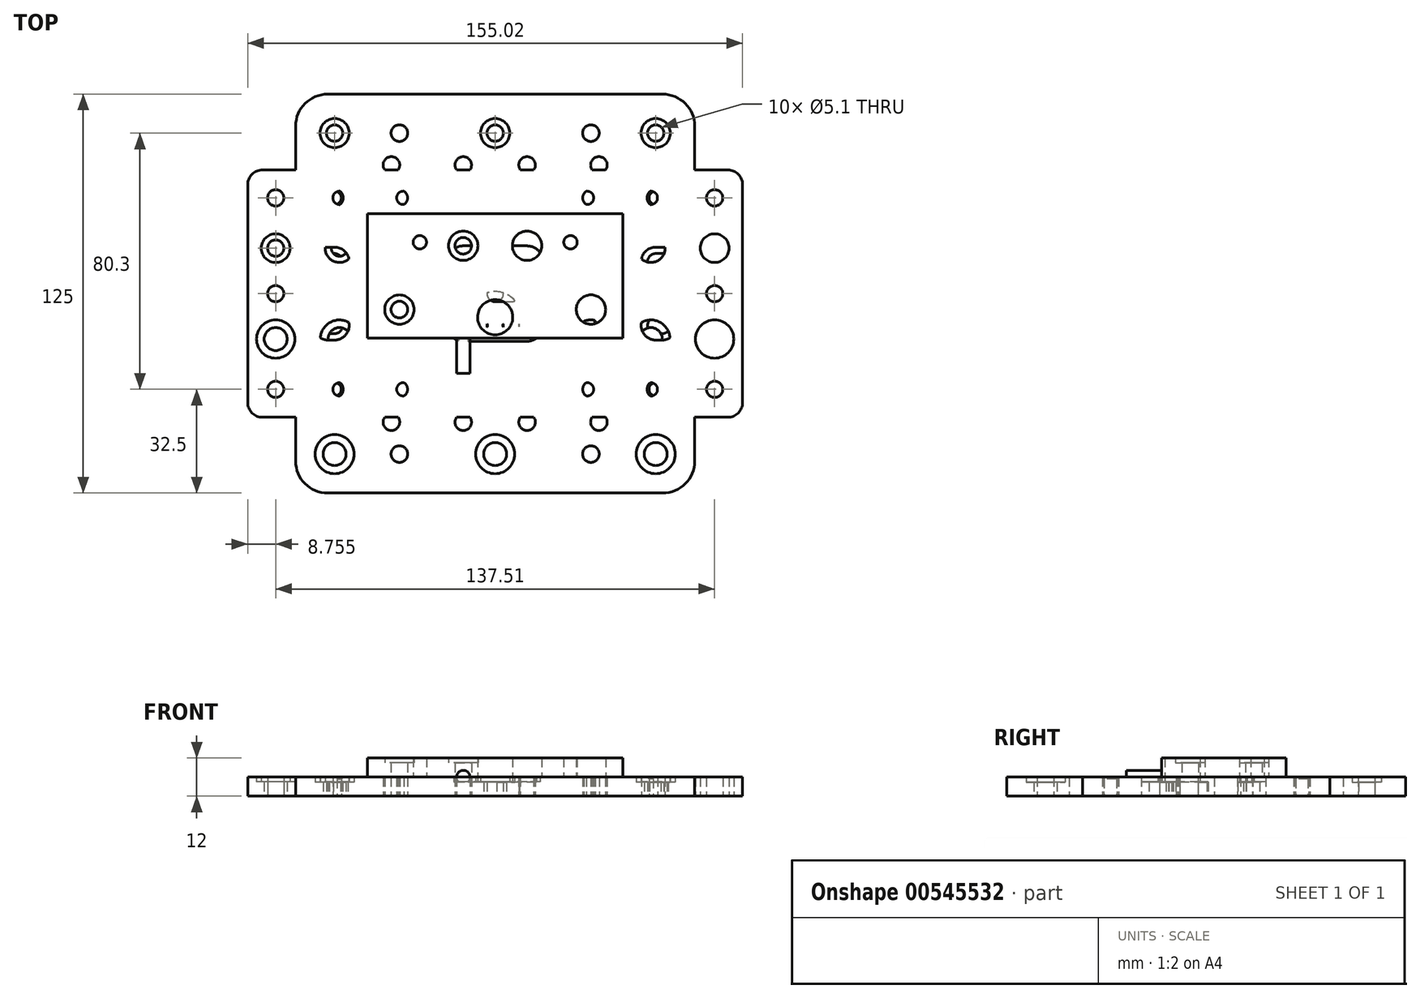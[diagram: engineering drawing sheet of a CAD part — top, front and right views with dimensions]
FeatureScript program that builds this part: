
annotation { "Feature Type Name" : "Feature", "Feature Type Description" : "" }
export const myFeature = defineFeature(function(context is Context, id is Id, definition is map)
    precondition{}
    {
        {
            assignVariable(context, id + "F0", {"name" : "CBeamEndPlateThickness", "anyValue" : 12});
        }
        {
            assignVariable(context, id + "F1", {"name" : "gantryPlateThickness", "anyValue" : 6});
        }
        {
            var Q0;
            Q0=qCreatedBy(makeId("Top.planeOp"),FACE);
            var sketch = newSketch(context, id + "F2", { "sketchPlane" : qUnion([Q0])});
            skLineSegment(sketch, "E0.bottom", {"start": v(-40, 25) * mm, "end": v(40, 25) * mm});
            skLineSegment(sketch, "E0.top", {"start": v(-40, -25) * mm, "end": v(40, -25) * mm});
            skLineSegment(sketch, "E0.left", {"start": v(-40, 25) * mm, "end": v(-40, -25) * mm});
            skLineSegment(sketch, "E0.right", {"start": v(40, 25) * mm, "end": v(40, -25) * mm});
            skPoint(sketch, "E0.middle", {"position": v(0, 0) * mm});
            skCircle(sketch, "E1", {"center": v(0, -7.4) * mm, "radius": 5.5 * mm});
            skCircle(sketch, "E2", {"center": v(0, -7.4) * mm, "radius": 8.05 * mm});
            skCircle(sketch, "E3", {"center": v(-30, -5) * mm, "radius": 2.6 * mm});
            skCircle(sketch, "E4", {"center": v(-30, -5) * mm, "radius": 4.6 * mm});
            skCircle(sketch, "E5", {"center": v(-23.6, 16.1) * mm, "radius": 2.1 * mm});
            skCircle(sketch, "E6", {"center": v(-10, 15) * mm, "radius": 2.6 * mm});
            skCircle(sketch, "E7", {"center": v(-10, 15) * mm, "radius": 4.6 * mm});
            skLineSegment(sketch, "E8", {"start": v(0, 0) * mm, "end": v(0, 25) * mm, "construction": true});
            skCircle(sketch, "E9.MirrorC", {"center": v(10, 15) * mm, "radius": 4.6 * mm});
            skCircle(sketch, "E10.MirrorC", {"center": v(10, 15) * mm, "radius": 2.6 * mm});
            skCircle(sketch, "E11.MirrorC", {"center": v(23.6, 16.1) * mm, "radius": 2.1 * mm});
            skCircle(sketch, "E12.MirrorC", {"center": v(30, -5) * mm, "radius": 4.6 * mm});
            skCircle(sketch, "E13.MirrorC", {"center": v(30, -5) * mm, "radius": 2.6 * mm});
            skSolve(sketch);
        }
        {
            var Q0;
            Q0=makeQuery(id+"F2.imprint","IMPRINT",FACE,{"disambiguationData":[TD([[makeQuery(id+"F2.imprint","IMPRINT",EDGE,{"derivedFrom":sQuery(id+"F2.wireOp",EDGE,"E0.bottom")}),-1.0]])]});
            extrude(context, id + "F3", {"entities" : qUnion([Q0]), "depth" : (getVariable(context, 'CBeamEndPlateThickness')) * mm, "offsetDistance" : 25 * mm});
        }
        {
            var Q0;
            Q0=makeQuery(id+"F2.imprint","IMPRINT",FACE,{"disambiguationData":[TD([[makeQuery(id+"F2.imprint","IMPRINT",EDGE,{"derivedFrom":sQuery(id+"F2.wireOp",EDGE,"E3")}),-1.0]])]});
            var Q1;
            Q1=makeQuery(id+"F2.imprint","IMPRINT",FACE,{"disambiguationData":[TD([[makeQuery(id+"F2.imprint","IMPRINT",EDGE,{"derivedFrom":sQuery(id+"F2.wireOp",EDGE,"E6")}),-1.0]])]});
            var Q2;
            Q2=makeQuery(id+"F2.imprint","IMPRINT",FACE,{"disambiguationData":[TD([[makeQuery(id+"F2.imprint","IMPRINT",EDGE,{"derivedFrom":sQuery(id+"F2.wireOp",EDGE,"E9.MirrorC")}),-1.0]])]});
            var Q3;
            Q3=makeQuery(id+"F2.imprint","IMPRINT",FACE,{"disambiguationData":[TD([[makeQuery(id+"F2.imprint","IMPRINT",EDGE,{"derivedFrom":sQuery(id+"F2.wireOp",EDGE,"E12.MirrorC")}),-1.0]])]});
            extrude(context, id + "F4", {"entities" : qUnion([Q0, Q1, Q2, Q3]), "operationType" : NewBodyOperationType.ADD, "depth" : (getVariable(context, 'CBeamEndPlateThickness') - 1.55) * mm, "offsetDistance" : 25 * mm});
        }
        {
            var Q0;
            Q0=makeQuery(id+"F2.imprint","IMPRINT",FACE,{"disambiguationData":[TD([[makeQuery(id+"F2.imprint","IMPRINT",EDGE,{"derivedFrom":sQuery(id+"F2.wireOp",EDGE,"E1")}),-1.0]])]});
            extrude(context, id + "F5", {"entities" : qUnion([Q0]), "operationType" : NewBodyOperationType.ADD, "depth" : (getVariable(context, 'CBeamEndPlateThickness')) * mm, "offsetDistance" : 25 * mm, "hasSecondDirection" : true, "secondDirectionOppositeDirection" : false, "secondDirectionDepth" : 4.5 * mm});
        }
        {
            var Q0;
            Q0=makeQuery(id+"F3.opExtrude","SWEPT_FACE",FACE,{"disambiguationData":[OSD([sQuery(id+"F2.wireOp",EDGE,"E0.top")])]});
            var sketch = newSketch(context, id + "F6", { "sketchPlane" : qUnion([Q0])});
            skCircle(sketch, "E14", {"center": v(10, 6) * mm, "radius": 2.1 * mm});
            skLineSegment(sketch, "E15", {"start": v(0, 0) * mm, "end": v(0, 12) * mm, "construction": true});
            skCircle(sketch, "E16.MirrorC", {"center": v(-10, 6) * mm, "radius": 2.1 * mm});
            skPoint(sketch, "E17", {"position": v(0, 6) * mm});
            skSolve(sketch);
        }
        {
            var Q0;
            Q0=makeQuery(id+"F6.imprint","IMPRINT",FACE,{"disambiguationData":[TD([[makeQuery(id+"F6.imprint","IMPRINT",EDGE,{"derivedFrom":sQuery(id+"F6.wireOp",EDGE,"E14")}),1.0]])]});
            var Q1;
            Q1=makeQuery(id+"F6.imprint","IMPRINT",FACE,{"disambiguationData":[TD([[makeQuery(id+"F6.imprint","IMPRINT",EDGE,{"derivedFrom":sQuery(id+"F6.wireOp",EDGE,"E16.MirrorC")}),-1.0]])]});
            extrude(context, id + "F7", {"entities" : qUnion([Q0, Q1]), "operationType" : NewBodyOperationType.REMOVE, "oppositeDirection" : true, "depth" : 11 * mm, "offsetDistance" : 25 * mm});
        }
        {
            var Q0;
            Q0=qCreatedBy(makeId("Top.planeOp"),FACE);
            var sketch = newSketch(context, id + "F8", { "sketchPlane" : qUnion([Q0])});
            skLineSegment(sketch, "E18.bottom", {"start": v(33.94, -38.57) * mm, "end": v(-33.94, -38.58) * mm});
            skLineSegment(sketch, "E18.top", {"start": v(33.94, 38.58) * mm, "end": v(-33.94, 38.57) * mm});
            skLineSegment(sketch, "E18.left", {"start": v(38.57, -33.94) * mm, "end": v(38.57, 33.94) * mm});
            skLineSegment(sketch, "E18.right", {"start": v(-38.58, -33.94) * mm, "end": v(-38.58, 33.94) * mm});
            skPoint(sketch, "E18.middle", {"position": v(0, 0) * mm});
            skPoint(sketch, "E19.visualSharp", {"position": v(-38.57, 38.57) * mm});
            skArc(sketch, "E19.filletArc", {"start": v(-33.94, 38.57) * mm, "mid": v(-37.22, 37.22) * mm, "end": v(-38.58, 33.94) * mm});
            skPoint(sketch, "E20.visualSharp", {"position": v(38.58, 38.58) * mm});
            skArc(sketch, "E20.filletArc", {"start": v(38.57, 33.94) * mm, "mid": v(37.22, 37.22) * mm, "end": v(33.94, 38.58) * mm});
            skPoint(sketch, "E21.visualSharp", {"position": v(38.57, -38.57) * mm});
            skArc(sketch, "E21.filletArc", {"start": v(33.94, -38.57) * mm, "mid": v(37.22, -37.22) * mm, "end": v(38.57, -33.94) * mm});
            skPoint(sketch, "E22.visualSharp", {"position": v(-38.58, -38.58) * mm});
            skArc(sketch, "E22.filletArc", {"start": v(-38.58, -33.94) * mm, "mid": v(-37.22, -37.22) * mm, "end": v(-33.94, -38.58) * mm});
            skCircle(sketch, "E23", {"center": v(-30, -30) * mm, "radius": 2.55 * mm});
            skCircle(sketch, "E24.0.1.0", {"center": v(-30, 0) * mm, "radius": 2.55 * mm});
            skCircle(sketch, "E24.0.2.0", {"center": v(-30, 30) * mm, "radius": 2.55 * mm});
            skCircle(sketch, "E24.1.0.0", {"center": v(30, -30) * mm, "radius": 2.55 * mm});
            skCircle(sketch, "E24.1.1.0", {"center": v(30, 0) * mm, "radius": 2.55 * mm});
            skCircle(sketch, "E24.1.2.0", {"center": v(30, 30) * mm, "radius": 2.55 * mm});
            skLineSegment(sketch, "E24.direction1", {"start": v(-30, -30) * mm, "end": v(30, -30) * mm, "construction": true});
            skLineSegment(sketch, "E24.direction2", {"start": v(-30, -30) * mm, "end": v(-30, 0) * mm, "construction": true});
            skLineSegment(sketch, "E25", {"start": v(0, 0) * mm, "end": v(0, 38.58) * mm, "construction": true});
            skLineSegment(sketch, "E26", {"start": v(0, 0) * mm, "end": v(-38.58, 0) * mm, "construction": true});
            skCircle(sketch, "E27", {"center": v(-20, 10) * mm, "radius": 2.55 * mm});
            skCircle(sketch, "E28.MirrorC", {"center": v(-20, -10) * mm, "radius": 2.55 * mm});
            skCircle(sketch, "E29.MirrorC", {"center": v(20, 10) * mm, "radius": 2.55 * mm});
            skCircle(sketch, "E30.MirrorC", {"center": v(20, -10) * mm, "radius": 2.55 * mm});
            skCircle(sketch, "E31", {"center": v(-10, 0) * mm, "radius": 2.55 * mm});
            skCircle(sketch, "E32", {"center": v(0, 10) * mm, "radius": 2.55 * mm});
            skCircle(sketch, "E33", {"center": v(10, 10) * mm, "radius": 2.55 * mm});
            skCircle(sketch, "E34.MirrorC", {"center": v(0, -10) * mm, "radius": 2.55 * mm});
            skCircle(sketch, "E35.MirrorC", {"center": v(10, -10) * mm, "radius": 2.55 * mm});
            skLineSegment(sketch, "E36", {"start": v(0, 0) * mm, "end": v(10, 0) * mm, "construction": true});
            skArc(sketch, "E37.0.startCap", {"start": v(0, -2.55) * mm, "mid": v(-2.55, 0) * mm, "end": v(0, 2.55) * mm});
            skArc(sketch, "E37.0.endCap", {"start": v(10, 2.55) * mm, "mid": v(12.55, 0) * mm, "end": v(10, -2.55) * mm});
            skLineSegment(sketch, "E37.0.left", {"start": v(0, 2.55) * mm, "end": v(10, 2.55) * mm});
            skLineSegment(sketch, "E37.0.right", {"start": v(0, -2.55) * mm, "end": v(10, -2.55) * mm});
            skCircle(sketch, "E38", {"center": v(-10, -30) * mm, "radius": 2.1 * mm});
            skCircle(sketch, "E39.MirrorC", {"center": v(-10, 30) * mm, "radius": 2.1 * mm});
            skCircle(sketch, "E40.MirrorC", {"center": v(10, 30) * mm, "radius": 2.1 * mm});
            skCircle(sketch, "E41.MirrorC", {"center": v(10, -30) * mm, "radius": 2.1 * mm});
            skCircle(sketch, "E42", {"center": v(-20, 20) * mm, "radius": 2.1 * mm});
            skCircle(sketch, "E43", {"center": v(0, 20) * mm, "radius": 2.55 * mm});
            skCircle(sketch, "E44.MirrorC", {"center": v(20, 20) * mm, "radius": 2.1 * mm});
            skCircle(sketch, "E45.MirrorC", {"center": v(-20, -20) * mm, "radius": 2.1 * mm});
            skCircle(sketch, "E46.MirrorC", {"center": v(0, -20) * mm, "radius": 2.55 * mm});
            skCircle(sketch, "E47.MirrorC", {"center": v(20, -20) * mm, "radius": 2.1 * mm});
            skCircle(sketch, "E48", {"center": v(-30, -14.25) * mm, "radius": 3.6 * mm});
            skCircle(sketch, "E49", {"center": v(-30, -14.25) * mm, "radius": 6 * mm});
            skCircle(sketch, "E50.MirrorC", {"center": v(30, -14.25) * mm, "radius": 3.6 * mm});
            skCircle(sketch, "E51.MirrorC", {"center": v(30, -14.25) * mm, "radius": 6 * mm});
            skCircle(sketch, "E52", {"center": v(-30, 14.25) * mm, "radius": 2.55 * mm});
            skCircle(sketch, "E53", {"center": v(-30, 14.25) * mm, "radius": 4.5 * mm});
            skCircle(sketch, "E54.MirrorC", {"center": v(30, 14.25) * mm, "radius": 4.5 * mm});
            skCircle(sketch, "E55.MirrorC", {"center": v(30, 14.25) * mm, "radius": 2.55 * mm});
            skLineSegment(sketch, "E56.bottom", {"start": v(10.03, -14.95) * mm, "end": v(-10.03, -14.95) * mm});
            skLineSegment(sketch, "E56.top", {"start": v(10.03, 14.95) * mm, "end": v(-10.03, 14.95) * mm});
            skLineSegment(sketch, "E56.left", {"start": v(14.95, -10.03) * mm, "end": v(14.95, 10.03) * mm});
            skLineSegment(sketch, "E56.right", {"start": v(-14.95, -10.03) * mm, "end": v(-14.95, 10.03) * mm});
            skPoint(sketch, "E57.visualSharp", {"position": v(-14.95, 14.95) * mm});
            skArc(sketch, "E57.filletArc", {"start": v(-10.03, 14.95) * mm, "mid": v(-13.5, 13.5) * mm, "end": v(-14.95, 10.03) * mm});
            skPoint(sketch, "E58.visualSharp", {"position": v(14.95, 14.95) * mm});
            skArc(sketch, "E58.filletArc", {"start": v(14.95, 10.03) * mm, "mid": v(13.5, 13.5) * mm, "end": v(10.03, 14.95) * mm});
            skPoint(sketch, "E59.visualSharp", {"position": v(14.95, -14.95) * mm});
            skArc(sketch, "E59.filletArc", {"start": v(10.03, -14.95) * mm, "mid": v(13.5, -13.5) * mm, "end": v(14.95, -10.03) * mm});
            skPoint(sketch, "E60.visualSharp", {"position": v(-14.95, -14.95) * mm});
            skArc(sketch, "E60.filletArc", {"start": v(-14.95, -10.03) * mm, "mid": v(-13.5, -13.5) * mm, "end": v(-10.03, -14.95) * mm});
            skSolve(sketch);
        }
        {
            var Q0;
            Q0=makeQuery(id+"F8.imprint","IMPRINT",FACE,{"disambiguationData":[TD([[makeQuery(id+"F8.imprint","IMPRINT",EDGE,{"derivedFrom":sQuery(id+"F8.wireOp",EDGE,"E18.bottom")}),-1.0]])]});
            extrude(context, id + "F9", {"entities" : qUnion([Q0]), "depth" : (getVariable(context, 'gantryPlateThickness')) * mm, "offsetDistance" : 25 * mm});
        }
        {
            var Q0;
            Q0=makeQuery(id+"F8.imprint","IMPRINT",FACE,{"disambiguationData":[TD([[makeQuery(id+"F8.imprint","IMPRINT",EDGE,{"derivedFrom":sQuery(id+"F8.wireOp",EDGE,"E31")}),-1.0]])]});
            var Q1;
            Q1=makeQuery(id+"F8.imprint","IMPRINT",FACE,{"disambiguationData":[TD([[makeQuery(id+"F8.imprint","IMPRINT",EDGE,{"derivedFrom":sQuery(id+"F8.wireOp",EDGE,"E52")}),-1.0]])]});
            var Q2;
            Q2=makeQuery(id+"F8.imprint","IMPRINT",FACE,{"disambiguationData":[TD([[makeQuery(id+"F8.imprint","IMPRINT",EDGE,{"derivedFrom":sQuery(id+"F8.wireOp",EDGE,"E48")}),-1.0]])]});
            var Q3;
            Q3=makeQuery(id+"F8.imprint","IMPRINT",FACE,{"disambiguationData":[TD([[makeQuery(id+"F8.imprint","IMPRINT",EDGE,{"derivedFrom":sQuery(id+"F8.wireOp",EDGE,"E50.MirrorC")}),1.0]])]});
            var Q4;
            Q4=makeQuery(id+"F8.imprint","IMPRINT",FACE,{"disambiguationData":[TD([[makeQuery(id+"F8.imprint","IMPRINT",EDGE,{"derivedFrom":sQuery(id+"F8.wireOp",EDGE,"E54.MirrorC")}),-1.0]])]});
            extrude(context, id + "F10", {"entities" : qUnion([Q0, Q1, Q2, Q3, Q4]), "operationType" : NewBodyOperationType.ADD, "depth" : (getVariable(context, 'gantryPlateThickness') - 1.5) * mm, "offsetDistance" : 25 * mm});
        }
        {
            var Q0;
            Q0=qCreatedBy(makeId("Top.planeOp"),FACE);
            var sketch = newSketch(context, id + "F11", { "sketchPlane" : qUnion([Q0])});
            skLineSegment(sketch, "E61.bottom", {"start": v(72.87, -38.76) * mm, "end": v(-72.87, -38.76) * mm});
            skLineSegment(sketch, "E61.top", {"start": v(72.87, 38.76) * mm, "end": v(-72.87, 38.76) * mm});
            skLineSegment(sketch, "E61.left", {"start": v(77.51, -34.12) * mm, "end": v(77.51, 34.12) * mm});
            skLineSegment(sketch, "E61.right", {"start": v(-77.51, -34.12) * mm, "end": v(-77.51, 34.12) * mm});
            skPoint(sketch, "E61.middle", {"position": v(0, 0) * mm});
            skPoint(sketch, "E62.visualSharp", {"position": v(-77.51, 38.76) * mm});
            skArc(sketch, "E62.filletArc", {"start": v(-72.87, 38.76) * mm, "mid": v(-76.15, 37.4) * mm, "end": v(-77.51, 34.12) * mm});
            skPoint(sketch, "E63.visualSharp", {"position": v(77.51, 38.76) * mm});
            skArc(sketch, "E63.filletArc", {"start": v(77.51, 34.12) * mm, "mid": v(76.15, 37.4) * mm, "end": v(72.87, 38.76) * mm});
            skPoint(sketch, "E64.visualSharp", {"position": v(77.51, -38.76) * mm});
            skArc(sketch, "E64.filletArc", {"start": v(72.87, -38.76) * mm, "mid": v(76.15, -37.4) * mm, "end": v(77.51, -34.12) * mm});
            skPoint(sketch, "E65.visualSharp", {"position": v(-77.51, -38.76) * mm});
            skArc(sketch, "E65.filletArc", {"start": v(-77.51, -34.12) * mm, "mid": v(-76.15, -37.4) * mm, "end": v(-72.87, -38.76) * mm});
            skCircle(sketch, "E66", {"center": v(-68.76, 30) * mm, "radius": 2.55 * mm});
            skCircle(sketch, "E67", {"center": v(-48.76, 30) * mm, "radius": 2.1 * mm});
            skCircle(sketch, "E68", {"center": v(-28.76, 30) * mm, "radius": 2.1 * mm});
            skCircle(sketch, "E69", {"center": v(-8.76, 30) * mm, "radius": 2.55 * mm});
            skCircle(sketch, "E70", {"center": v(-58.76, 20) * mm, "radius": 2.1 * mm});
            skCircle(sketch, "E71", {"center": v(-38.76, 20) * mm, "radius": 2.55 * mm});
            skCircle(sketch, "E72", {"center": v(-20, 20) * mm, "radius": 2.1 * mm});
            skCircle(sketch, "E73", {"center": v(-28.76, 8.75) * mm, "radius": 2.55 * mm});
            skCircle(sketch, "E74", {"center": v(-68.76, 0) * mm, "radius": 2.55 * mm});
            skCircle(sketch, "E75", {"center": v(-48.76, 0) * mm, "radius": 2.55 * mm});
            skLineSegment(sketch, "E76", {"start": v(0, 0) * mm, "end": v(-77.51, 0) * mm, "construction": true});
            skLineSegment(sketch, "E77", {"start": v(0, 0) * mm, "end": v(0, 38.76) * mm, "construction": true});
            skCircle(sketch, "E78.MirrorC", {"center": v(8.75, 30) * mm, "radius": 2.55 * mm});
            skCircle(sketch, "E79.MirrorC", {"center": v(20, 20) * mm, "radius": 2.1 * mm});
            skCircle(sketch, "E80.MirrorC", {"center": v(28.75, 30) * mm, "radius": 2.1 * mm});
            skCircle(sketch, "E81.MirrorC", {"center": v(28.76, 8.76) * mm, "radius": 2.55 * mm});
            skCircle(sketch, "E82.MirrorC", {"center": v(38.76, 20) * mm, "radius": 2.55 * mm});
            skCircle(sketch, "E83.MirrorC", {"center": v(48.76, 30) * mm, "radius": 2.1 * mm});
            skCircle(sketch, "E84.MirrorC", {"center": v(48.76, 0) * mm, "radius": 2.55 * mm});
            skCircle(sketch, "E85.MirrorC", {"center": v(58.76, 20) * mm, "radius": 2.1 * mm});
            skCircle(sketch, "E86.MirrorC", {"center": v(68.76, 30) * mm, "radius": 2.55 * mm});
            skCircle(sketch, "E87.MirrorC", {"center": v(68.76, 0) * mm, "radius": 2.55 * mm});
            skCircle(sketch, "E88", {"center": v(-48.76, 14.25) * mm, "radius": 2.55 * mm});
            skCircle(sketch, "E89", {"center": v(-48.76, 14.25) * mm, "radius": 4.5 * mm});
            skCircle(sketch, "E90", {"center": v(-68.76, 14.25) * mm, "radius": 2.55 * mm});
            skCircle(sketch, "E91", {"center": v(-68.76, 14.25) * mm, "radius": 4.5 * mm});
            skCircle(sketch, "E92.MirrorC", {"center": v(48.76, 14.25) * mm, "radius": 4.5 * mm});
            skCircle(sketch, "E93.MirrorC", {"center": v(48.76, 14.25) * mm, "radius": 2.55 * mm});
            skCircle(sketch, "E94.MirrorC", {"center": v(68.76, 14.25) * mm, "radius": 4.5 * mm});
            skCircle(sketch, "E95.MirrorC", {"center": v(68.76, 14.25) * mm, "radius": 2.55 * mm});
            skCircle(sketch, "E96", {"center": v(-68.76, -14.25) * mm, "radius": 3.6 * mm});
            skCircle(sketch, "E97", {"center": v(-68.76, -14.25) * mm, "radius": 6 * mm});
            skCircle(sketch, "E98", {"center": v(-48.76, -14.25) * mm, "radius": 3.6 * mm});
            skCircle(sketch, "E99", {"center": v(-48.76, -14.25) * mm, "radius": 6 * mm});
            skCircle(sketch, "E100.MirrorC", {"center": v(48.76, -14.25) * mm, "radius": 3.6 * mm});
            skCircle(sketch, "E101.MirrorC", {"center": v(48.76, -14.25) * mm, "radius": 6 * mm});
            skCircle(sketch, "E102.MirrorC", {"center": v(68.76, -14.25) * mm, "radius": 6 * mm});
            skCircle(sketch, "E103.MirrorC", {"center": v(68.76, -14.25) * mm, "radius": 3.6 * mm});
            skCircle(sketch, "E104.MirrorC", {"center": v(-68.75, -30) * mm, "radius": 2.55 * mm});
            skCircle(sketch, "E105.MirrorC", {"center": v(-48.76, -30) * mm, "radius": 2.1 * mm});
            skCircle(sketch, "E106.MirrorC", {"center": v(-28.75, -30) * mm, "radius": 2.1 * mm});
            skCircle(sketch, "E107.MirrorC", {"center": v(-8.75, -30) * mm, "radius": 2.55 * mm});
            skCircle(sketch, "E108.MirrorC", {"center": v(8.76, -30) * mm, "radius": 2.55 * mm});
            skCircle(sketch, "E109.MirrorC", {"center": v(28.76, -30) * mm, "radius": 2.1 * mm});
            skCircle(sketch, "E110.MirrorC", {"center": v(48.76, -30) * mm, "radius": 2.1 * mm});
            skCircle(sketch, "E111.MirrorC", {"center": v(68.76, -30) * mm, "radius": 2.55 * mm});
            skCircle(sketch, "E112.MirrorC", {"center": v(58.76, -20) * mm, "radius": 2.1 * mm});
            skCircle(sketch, "E113.MirrorC", {"center": v(38.76, -20) * mm, "radius": 2.55 * mm});
            skCircle(sketch, "E114.MirrorC", {"center": v(20, -20) * mm, "radius": 2.1 * mm});
            skCircle(sketch, "E115.MirrorC", {"center": v(-20, -20) * mm, "radius": 2.1 * mm});
            skCircle(sketch, "E116.MirrorC", {"center": v(-38.76, -20) * mm, "radius": 2.55 * mm});
            skCircle(sketch, "E117.MirrorC", {"center": v(-58.76, -20) * mm, "radius": 2.1 * mm});
            skCircle(sketch, "E118.MirrorC", {"center": v(-28.75, -8.76) * mm, "radius": 2.55 * mm});
            skCircle(sketch, "E119.MirrorC", {"center": v(28.76, -8.75) * mm, "radius": 2.55 * mm});
            skLineSegment(sketch, "E120.bottom", {"start": v(15.04, -14.95) * mm, "end": v(-15.04, -14.95) * mm});
            skLineSegment(sketch, "E120.top", {"start": v(15.04, 14.95) * mm, "end": v(-15.04, 14.95) * mm});
            skLineSegment(sketch, "E120.left", {"start": v(19.98, -10) * mm, "end": v(19.98, 10) * mm});
            skLineSegment(sketch, "E120.right", {"start": v(-19.98, -10.01) * mm, "end": v(-19.98, 10) * mm});
            skPoint(sketch, "E121.visualSharp", {"position": v(-19.98, 14.95) * mm});
            skArc(sketch, "E121.filletArc", {"start": v(-15.04, 14.95) * mm, "mid": v(-18.53, 13.5) * mm, "end": v(-19.98, 10) * mm});
            skPoint(sketch, "E122.visualSharp", {"position": v(19.98, 14.95) * mm});
            skArc(sketch, "E122.filletArc", {"start": v(19.98, 10) * mm, "mid": v(18.53, 13.5) * mm, "end": v(15.04, 14.95) * mm});
            skPoint(sketch, "E123.visualSharp", {"position": v(19.98, -14.95) * mm});
            skArc(sketch, "E123.filletArc", {"start": v(15.04, -14.95) * mm, "mid": v(18.53, -13.5) * mm, "end": v(19.98, -10) * mm});
            skPoint(sketch, "E124.visualSharp", {"position": v(-19.98, -14.95) * mm});
            skArc(sketch, "E124.filletArc", {"start": v(-19.98, -10.01) * mm, "mid": v(-18.53, -13.5) * mm, "end": v(-15.04, -14.95) * mm});
            skLineSegment(sketch, "E125", {"start": v(5.03, 0) * mm, "end": v(-5.03, 0) * mm, "construction": true});
            skArc(sketch, "E126.0.startCap", {"start": v(5.03, 2.55) * mm, "mid": v(7.58, 0) * mm, "end": v(5.03, -2.55) * mm});
            skArc(sketch, "E126.0.endCap", {"start": v(-5.03, -2.55) * mm, "mid": v(-7.58, 0) * mm, "end": v(-5.03, 2.55) * mm});
            skLineSegment(sketch, "E126.0.left", {"start": v(5.03, -2.55) * mm, "end": v(-5.03, -2.55) * mm});
            skLineSegment(sketch, "E126.0.right", {"start": v(5.03, 2.55) * mm, "end": v(-5.03, 2.55) * mm});
            skCircle(sketch, "E127", {"center": v(-15, -10) * mm, "radius": 2.55 * mm});
            skCircle(sketch, "E128.0.1.0", {"center": v(-15, 10) * mm, "radius": 2.55 * mm});
            skCircle(sketch, "E128.1.0.0", {"center": v(-5, -10) * mm, "radius": 2.55 * mm});
            skCircle(sketch, "E128.1.1.0", {"center": v(-5, 10) * mm, "radius": 2.55 * mm});
            skCircle(sketch, "E128.2.0.0", {"center": v(5, -10) * mm, "radius": 2.55 * mm});
            skCircle(sketch, "E128.2.1.0", {"center": v(5, 10) * mm, "radius": 2.55 * mm});
            skCircle(sketch, "E128.3.0.0", {"center": v(15, -10) * mm, "radius": 2.55 * mm});
            skCircle(sketch, "E128.3.1.0", {"center": v(15, 10) * mm, "radius": 2.55 * mm});
            skLineSegment(sketch, "E128.direction1", {"start": v(-15, -10) * mm, "end": v(-5, -10) * mm, "construction": true});
            skLineSegment(sketch, "E128.direction2", {"start": v(-15, -10) * mm, "end": v(-15, 10) * mm, "construction": true});
            skCircle(sketch, "E129", {"center": v(-15, 0) * mm, "radius": 2.55 * mm});
            skCircle(sketch, "E130.MirrorC", {"center": v(15, 0) * mm, "radius": 2.55 * mm});
            skSolve(sketch);
        }
        {
            var Q0;
            Q0=makeQuery(id+"F11.imprint","IMPRINT",FACE,{"disambiguationData":[TD([[makeQuery(id+"F11.imprint","IMPRINT",EDGE,{"derivedFrom":sQuery(id+"F11.wireOp",EDGE,"E61.bottom")}),-1.0]])]});
            extrude(context, id + "F12", {"entities" : qUnion([Q0]), "depth" : (getVariable(context, 'gantryPlateThickness')) * mm, "offsetDistance" : 25 * mm});
        }
        {
            var Q0;
            Q0=makeQuery(id+"F11.imprint","IMPRINT",FACE,{"disambiguationData":[TD([[makeQuery(id+"F11.imprint","IMPRINT",EDGE,{"derivedFrom":sQuery(id+"F11.wireOp",EDGE,"E90")}),-1.0]])]});
            var Q1;
            Q1=makeQuery(id+"F11.imprint","IMPRINT",FACE,{"disambiguationData":[TD([[makeQuery(id+"F11.imprint","IMPRINT",EDGE,{"derivedFrom":sQuery(id+"F11.wireOp",EDGE,"E88")}),-1.0]])]});
            var Q2;
            Q2=makeQuery(id+"F11.imprint","IMPRINT",FACE,{"disambiguationData":[TD([[makeQuery(id+"F11.imprint","IMPRINT",EDGE,{"derivedFrom":sQuery(id+"F11.wireOp",EDGE,"E96")}),-1.0]])]});
            var Q3;
            Q3=makeQuery(id+"F11.imprint","IMPRINT",FACE,{"disambiguationData":[TD([[makeQuery(id+"F11.imprint","IMPRINT",EDGE,{"derivedFrom":sQuery(id+"F11.wireOp",EDGE,"E98")}),-1.0]])]});
            var Q4;
            Q4=makeQuery(id+"F11.imprint","IMPRINT",FACE,{"disambiguationData":[TD([[makeQuery(id+"F11.imprint","IMPRINT",EDGE,{"derivedFrom":sQuery(id+"F11.wireOp",EDGE,"E120.bottom")}),-1.0]])]});
            var Q5;
            Q5=makeQuery(id+"F11.imprint","IMPRINT",FACE,{"disambiguationData":[TD([[makeQuery(id+"F11.imprint","IMPRINT",EDGE,{"derivedFrom":sQuery(id+"F11.wireOp",EDGE,"E100.MirrorC")}),1.0]])]});
            var Q6;
            Q6=makeQuery(id+"F11.imprint","IMPRINT",FACE,{"disambiguationData":[TD([[makeQuery(id+"F11.imprint","IMPRINT",EDGE,{"derivedFrom":sQuery(id+"F11.wireOp",EDGE,"E102.MirrorC")}),-1.0]])]});
            var Q7;
            Q7=makeQuery(id+"F11.imprint","IMPRINT",FACE,{"disambiguationData":[TD([[makeQuery(id+"F11.imprint","IMPRINT",EDGE,{"derivedFrom":sQuery(id+"F11.wireOp",EDGE,"E94.MirrorC")}),-1.0]])]});
            var Q8;
            Q8=makeQuery(id+"F11.imprint","IMPRINT",FACE,{"disambiguationData":[TD([[makeQuery(id+"F11.imprint","IMPRINT",EDGE,{"derivedFrom":sQuery(id+"F11.wireOp",EDGE,"E92.MirrorC")}),-1.0]])]});
            extrude(context, id + "F13", {"entities" : qUnion([Q0, Q1, Q2, Q3, Q4, Q5, Q6, Q7, Q8]), "operationType" : NewBodyOperationType.ADD, "depth" : (getVariable(context, 'gantryPlateThickness') - 1.5) * mm, "offsetDistance" : 25 * mm});
        }
        {
            var Q0;
            Q0=qCreatedBy(makeId("Top.planeOp"),FACE);
            var sketch = newSketch(context, id + "F14", { "sketchPlane" : qUnion([Q0])});
            skLineSegment(sketch, "E131.bottom", {"start": v(-52.5, 62.5) * mm, "end": v(52.5, 62.5) * mm});
            skLineSegment(sketch, "E131.top", {"start": v(-52.5, -62.5) * mm, "end": v(52.5, -62.5) * mm});
            skLineSegment(sketch, "E131.left", {"start": v(-62.5, 52.5) * mm, "end": v(-62.5, -52.5) * mm});
            skLineSegment(sketch, "E131.right", {"start": v(62.5, 52.5) * mm, "end": v(62.5, -52.5) * mm});
            skPoint(sketch, "E131.middle", {"position": v(0, 0) * mm});
            skPoint(sketch, "E132.visualSharp", {"position": v(-62.5, 62.5) * mm});
            skArc(sketch, "E132.filletArc", {"start": v(-52.5, 62.5) * mm, "mid": v(-59.57, 59.57) * mm, "end": v(-62.5, 52.5) * mm});
            skPoint(sketch, "E133.visualSharp", {"position": v(62.5, 62.5) * mm});
            skArc(sketch, "E133.filletArc", {"start": v(62.5, 52.5) * mm, "mid": v(59.57, 59.57) * mm, "end": v(52.5, 62.5) * mm});
            skPoint(sketch, "E134.visualSharp", {"position": v(62.5, -62.5) * mm});
            skArc(sketch, "E134.filletArc", {"start": v(52.5, -62.5) * mm, "mid": v(59.57, -59.57) * mm, "end": v(62.5, -52.5) * mm});
            skPoint(sketch, "E135.visualSharp", {"position": v(-62.5, -62.5) * mm});
            skArc(sketch, "E135.filletArc", {"start": v(-62.5, -52.5) * mm, "mid": v(-59.57, -59.57) * mm, "end": v(-52.5, -62.5) * mm});
            skCircle(sketch, "E136", {"center": v(-30, -30) * mm, "radius": 2.6 * mm});
            skCircle(sketch, "E137", {"center": v(-30, -10) * mm, "radius": 2.6 * mm});
            skCircle(sketch, "E138.0.1.0", {"center": v(-30, 10) * mm, "radius": 2.6 * mm});
            skCircle(sketch, "E138.1.0.0", {"center": v(-10, -10) * mm, "radius": 2.6 * mm});
            skCircle(sketch, "E138.1.1.0", {"center": v(-10, 10) * mm, "radius": 2.6 * mm});
            skCircle(sketch, "E138.2.0.0", {"center": v(10, -10) * mm, "radius": 2.6 * mm});
            skCircle(sketch, "E138.2.1.0", {"center": v(10, 10) * mm, "radius": 2.6 * mm});
            skCircle(sketch, "E138.3.0.0", {"center": v(30, -10) * mm, "radius": 2.6 * mm});
            skCircle(sketch, "E138.3.1.0", {"center": v(30, 10) * mm, "radius": 2.6 * mm});
            skLineSegment(sketch, "E138.direction1", {"start": v(-30, -10) * mm, "end": v(-10, -10) * mm, "construction": true});
            skLineSegment(sketch, "E138.direction2", {"start": v(-30, -10) * mm, "end": v(-30, 10) * mm, "construction": true});
            skCircle(sketch, "E139.0.1.0", {"center": v(-30, 0) * mm, "radius": 2.6 * mm});
            skCircle(sketch, "E139.0.2.0", {"center": v(-30, 30) * mm, "radius": 2.6 * mm});
            skCircle(sketch, "E139.1.0.0", {"center": v(0, -30) * mm, "radius": 2.6 * mm});
            skCircle(sketch, "E139.1.1.0", {"center": v(0, 0) * mm, "radius": 2.6 * mm});
            skCircle(sketch, "E139.1.2.0", {"center": v(0, 30) * mm, "radius": 2.6 * mm});
            skCircle(sketch, "E139.2.0.0", {"center": v(30, -30) * mm, "radius": 2.6 * mm});
            skCircle(sketch, "E139.2.1.0", {"center": v(30, 0) * mm, "radius": 2.6 * mm});
            skCircle(sketch, "E139.2.2.0", {"center": v(30, 30) * mm, "radius": 2.6 * mm});
            skLineSegment(sketch, "E139.direction1", {"start": v(-30, -30) * mm, "end": v(0, -30) * mm, "construction": true});
            skLineSegment(sketch, "E139.direction2", {"start": v(-30, -30) * mm, "end": v(-30, 0) * mm, "construction": true});
            skCircle(sketch, "E140", {"center": v(-50.3, -30) * mm, "radius": 2.1 * mm});
            skCircle(sketch, "E141.0.1.0", {"center": v(-50.3, 30) * mm, "radius": 2.1 * mm});
            skCircle(sketch, "E141.1.0.0", {"center": v(50.3, -30) * mm, "radius": 2.1 * mm});
            skCircle(sketch, "E141.1.1.0", {"center": v(50.3, 30) * mm, "radius": 2.1 * mm});
            skLineSegment(sketch, "E141.direction1", {"start": v(-50.3, -30) * mm, "end": v(50.3, -30) * mm, "construction": true});
            skLineSegment(sketch, "E141.direction2", {"start": v(-50.3, -30) * mm, "end": v(-50.3, 30) * mm, "construction": true});
            skLineSegment(sketch, "E142", {"start": v(0, 0) * mm, "end": v(-10, 0) * mm, "construction": true});
            skLineSegment(sketch, "E143", {"start": v(0, 0) * mm, "end": v(0, -10) * mm, "construction": true});
            skCircle(sketch, "E144", {"center": v(-10, -40.3) * mm, "radius": 2.6 * mm});
            skCircle(sketch, "E145.0.1.0", {"center": v(-10, 40.3) * mm, "radius": 2.6 * mm});
            skCircle(sketch, "E145.1.0.0", {"center": v(-32.5, -40.3) * mm, "radius": 2.6 * mm});
            skCircle(sketch, "E145.1.1.0", {"center": v(-32.5, 40.3) * mm, "radius": 2.6 * mm});
            skLineSegment(sketch, "E145.direction1", {"start": v(-10, -40.3) * mm, "end": v(-32.5, -40.3) * mm, "construction": true});
            skLineSegment(sketch, "E145.direction2", {"start": v(-10, -40.3) * mm, "end": v(-10, 40.3) * mm, "construction": true});
            skCircle(sketch, "E146.MirrorC", {"center": v(32.5, -40.3) * mm, "radius": 2.6 * mm});
            skCircle(sketch, "E147.MirrorC", {"center": v(10, -40.3) * mm, "radius": 2.6 * mm});
            skCircle(sketch, "E148.MirrorC", {"center": v(32.5, 40.3) * mm, "radius": 2.6 * mm});
            skCircle(sketch, "E149.MirrorC", {"center": v(10, 40.3) * mm, "radius": 2.6 * mm});
            skCircle(sketch, "E150", {"center": v(-50.3, -50.3) * mm, "radius": 3.6 * mm});
            skCircle(sketch, "E151", {"center": v(-30, -50.3) * mm, "radius": 2.6 * mm});
            skCircle(sketch, "E152.MirrorC", {"center": v(30, -50.3) * mm, "radius": 2.6 * mm});
            skCircle(sketch, "E153.MirrorC", {"center": v(-30, 50.3) * mm, "radius": 2.6 * mm});
            skCircle(sketch, "E154.MirrorC", {"center": v(30, 50.3) * mm, "radius": 2.6 * mm});
            skCircle(sketch, "E155", {"center": v(-50.3, 50.3) * mm, "radius": 2.55 * mm});
            skCircle(sketch, "E156", {"center": v(-50.3, -50.3) * mm, "radius": 6.12 * mm});
            skCircle(sketch, "E157.1.0.0", {"center": v(0, -50.3) * mm, "radius": 6.12 * mm});
            skCircle(sketch, "E157.1.0.1", {"center": v(0, -50.3) * mm, "radius": 3.6 * mm});
            skCircle(sketch, "E157.2.0.0", {"center": v(50.3, -50.3) * mm, "radius": 6.12 * mm});
            skCircle(sketch, "E157.2.0.1", {"center": v(50.3, -50.3) * mm, "radius": 3.6 * mm});
            skLineSegment(sketch, "E157.direction1", {"start": v(-50.3, -50.3) * mm, "end": v(0, -50.3) * mm, "construction": true});
            skCircle(sketch, "E158", {"center": v(-50.3, 50.3) * mm, "radius": 4.57 * mm});
            skCircle(sketch, "E159.1.0.0", {"center": v(0, 50.3) * mm, "radius": 2.55 * mm});
            skCircle(sketch, "E159.1.0.1", {"center": v(0, 50.3) * mm, "radius": 4.57 * mm});
            skCircle(sketch, "E159.2.0.0", {"center": v(50.3, 50.3) * mm, "radius": 2.55 * mm});
            skCircle(sketch, "E159.2.0.1", {"center": v(50.3, 50.3) * mm, "radius": 4.57 * mm});
            skLineSegment(sketch, "E159.direction1", {"start": v(-50.3, 50.3) * mm, "end": v(0, 50.3) * mm, "construction": true});
            skLineSegment(sketch, "E160", {"start": v(-50.3, -10) * mm, "end": v(-52.3, -10) * mm, "construction": true});
            skArc(sketch, "E161.0.startCap", {"start": v(-50.3, -7.45) * mm, "mid": v(-47.75, -10) * mm, "end": v(-50.3, -12.55) * mm});
            skArc(sketch, "E161.0.endCap", {"start": v(-52.3, -12.55) * mm, "mid": v(-54.85, -10) * mm, "end": v(-52.3, -7.45) * mm});
            skLineSegment(sketch, "E161.0.left", {"start": v(-50.3, -12.55) * mm, "end": v(-52.3, -12.55) * mm});
            skLineSegment(sketch, "E161.0.right", {"start": v(-50.3, -7.45) * mm, "end": v(-52.3, -7.45) * mm});
            skLineSegment(sketch, "E162.0", {"start": v(-50.3, -14.57) * mm, "end": v(-52.3, -14.57) * mm});
            skArc(sketch, "E162.1", {"start": v(-50.3, -5.43) * mm, "mid": v(-45.73, -10) * mm, "end": v(-50.3, -14.57) * mm});
            skLineSegment(sketch, "E162.2", {"start": v(-50.3, -5.43) * mm, "end": v(-52.3, -5.43) * mm});
            skArc(sketch, "E162.3", {"start": v(-52.3, -14.57) * mm, "mid": v(-56.87, -10) * mm, "end": v(-52.3, -5.43) * mm});
            skLineSegment(sketch, "E163.MirrorCS", {"start": v(-50.3, 12.55) * mm, "end": v(-52.3, 12.55) * mm});
            skLineSegment(sketch, "E164.MirrorCS", {"start": v(-50.3, 14.57) * mm, "end": v(-52.3, 14.57) * mm});
            skArc(sketch, "E165.MirrorCS", {"start": v(-52.3, 14.57) * mm, "mid": v(-56.87, 10) * mm, "end": v(-52.3, 5.43) * mm});
            skArc(sketch, "E166.MirrorCS", {"start": v(-52.3, 12.55) * mm, "mid": v(-54.85, 10) * mm, "end": v(-52.3, 7.45) * mm});
            skArc(sketch, "E167.MirrorCS", {"start": v(-50.3, 7.45) * mm, "mid": v(-47.75, 10) * mm, "end": v(-50.3, 12.55) * mm});
            skLineSegment(sketch, "E168.MirrorCS", {"start": v(-50.3, 7.45) * mm, "end": v(-52.3, 7.45) * mm});
            skLineSegment(sketch, "E169.MirrorCS", {"start": v(-50.3, 5.43) * mm, "end": v(-52.3, 5.43) * mm});
            skArc(sketch, "E170.MirrorCS", {"start": v(-50.3, 5.43) * mm, "mid": v(-45.73, 10) * mm, "end": v(-50.3, 14.57) * mm});
            skLineSegment(sketch, "E171.MirrorCS", {"start": v(50.3, -12.55) * mm, "end": v(52.3, -12.55) * mm});
            skLineSegment(sketch, "E172.MirrorCS", {"start": v(50.3, -14.57) * mm, "end": v(52.3, -14.57) * mm});
            skArc(sketch, "E173.MirrorCS", {"start": v(52.3, 12.55) * mm, "mid": v(54.85, 10) * mm, "end": v(52.3, 7.45) * mm});
            skArc(sketch, "E174.MirrorCS", {"start": v(52.3, 14.57) * mm, "mid": v(56.87, 10) * mm, "end": v(52.3, 5.43) * mm});
            skLineSegment(sketch, "E175.MirrorCS", {"start": v(50.3, 12.55) * mm, "end": v(52.3, 12.55) * mm});
            skLineSegment(sketch, "E176.MirrorCS", {"start": v(50.3, 7.45) * mm, "end": v(52.3, 7.45) * mm});
            skLineSegment(sketch, "E177.MirrorCS", {"start": v(50.3, -5.43) * mm, "end": v(52.3, -5.43) * mm});
            skArc(sketch, "E178.MirrorCS", {"start": v(50.3, 5.43) * mm, "mid": v(45.73, 10) * mm, "end": v(50.3, 14.57) * mm});
            skArc(sketch, "E179.MirrorCS", {"start": v(50.3, -5.43) * mm, "mid": v(45.73, -10) * mm, "end": v(50.3, -14.57) * mm});
            skArc(sketch, "E180.MirrorCS", {"start": v(50.3, -7.45) * mm, "mid": v(47.75, -10) * mm, "end": v(50.3, -12.55) * mm});
            skLineSegment(sketch, "E181.MirrorCS", {"start": v(50.3, -7.45) * mm, "end": v(52.3, -7.45) * mm});
            skArc(sketch, "E182.MirrorCS", {"start": v(52.3, -12.55) * mm, "mid": v(54.85, -10) * mm, "end": v(52.3, -7.45) * mm});
            skArc(sketch, "E183.MirrorCS", {"start": v(50.3, 7.45) * mm, "mid": v(47.75, 10) * mm, "end": v(50.3, 12.55) * mm});
            skLineSegment(sketch, "E184.MirrorCS", {"start": v(50.3, 14.57) * mm, "end": v(52.3, 14.57) * mm});
            skLineSegment(sketch, "E185.MirrorCS", {"start": v(50.3, 5.43) * mm, "end": v(52.3, 5.43) * mm});
            skArc(sketch, "E186.MirrorCS", {"start": v(52.3, -14.57) * mm, "mid": v(56.87, -10) * mm, "end": v(52.3, -5.43) * mm});
            skLineSegment(sketch, "E187.bottom", {"start": v(14.7, 17.5) * mm, "end": v(-14.7, 17.5) * mm});
            skLineSegment(sketch, "E187.top", {"start": v(14.7, -17.5) * mm, "end": v(-14.7, -17.5) * mm});
            skLineSegment(sketch, "E187.left", {"start": v(17.5, 14.7) * mm, "end": v(17.5, -14.7) * mm});
            skLineSegment(sketch, "E187.right", {"start": v(-17.5, 14.7) * mm, "end": v(-17.5, -14.7) * mm});
            skPoint(sketch, "E188.visualSharp", {"position": v(-17.5, 17.5) * mm});
            skArc(sketch, "E188.filletArc", {"start": v(-14.7, 17.5) * mm, "mid": v(-16.68, 16.68) * mm, "end": v(-17.5, 14.7) * mm});
            skPoint(sketch, "E189.visualSharp", {"position": v(17.5, 17.5) * mm});
            skArc(sketch, "E189.filletArc", {"start": v(17.5, 14.7) * mm, "mid": v(16.68, 16.68) * mm, "end": v(14.7, 17.5) * mm});
            skPoint(sketch, "E190.visualSharp", {"position": v(17.5, -17.5) * mm});
            skArc(sketch, "E190.filletArc", {"start": v(14.7, -17.5) * mm, "mid": v(16.68, -16.68) * mm, "end": v(17.5, -14.7) * mm});
            skPoint(sketch, "E191.visualSharp", {"position": v(-17.5, -17.5) * mm});
            skArc(sketch, "E191.filletArc", {"start": v(-17.5, -14.7) * mm, "mid": v(-16.68, -16.68) * mm, "end": v(-14.7, -17.5) * mm});
            skSolve(sketch);
        }
        {
            var Q0;
            Q0=makeQuery(id+"F14.imprint","IMPRINT",FACE,{"disambiguationData":[TD([[makeQuery(id+"F14.imprint","IMPRINT",EDGE,{"derivedFrom":sQuery(id+"F14.wireOp",EDGE,"E131.bottom")}),-1.0]])]});
            extrude(context, id + "F15", {"entities" : qUnion([Q0]), "depth" : 6 * mm, "offsetDistance" : 25 * mm});
        }
        {
            var Q0;
            Q0=makeQuery(id+"F14.imprint","IMPRINT",FACE,{"disambiguationData":[TD([[makeQuery(id+"F14.imprint","IMPRINT",EDGE,{"derivedFrom":sQuery(id+"F14.wireOp",EDGE,"E138.1.0.0")}),-1.0]])]});
            var Q1;
            Q1=makeQuery(id+"F14.imprint","IMPRINT",FACE,{"disambiguationData":[TD([[makeQuery(id+"F14.imprint","IMPRINT",EDGE,{"derivedFrom":sQuery(id+"F14.wireOp",EDGE,"E159.1.0.0")}),-1.0]])]});
            var Q2;
            Q2=makeQuery(id+"F14.imprint","IMPRINT",FACE,{"disambiguationData":[TD([[makeQuery(id+"F14.imprint","IMPRINT",EDGE,{"derivedFrom":sQuery(id+"F14.wireOp",EDGE,"E155")}),-1.0]])]});
            var Q3;
            Q3=makeQuery(id+"F14.imprint","IMPRINT",FACE,{"disambiguationData":[TD([[makeQuery(id+"F14.imprint","IMPRINT",EDGE,{"derivedFrom":sQuery(id+"F14.wireOp",EDGE,"E163.MirrorCS")}),-1.0]])]});
            var Q4;
            Q4=makeQuery(id+"F14.imprint","IMPRINT",FACE,{"disambiguationData":[TD([[makeQuery(id+"F14.imprint","IMPRINT",EDGE,{"derivedFrom":sQuery(id+"F14.wireOp",EDGE,"E161.0.startCap")}),1.0]])]});
            var Q5;
            Q5=makeQuery(id+"F14.imprint","IMPRINT",FACE,{"disambiguationData":[TD([[makeQuery(id+"F14.imprint","IMPRINT",EDGE,{"derivedFrom":sQuery(id+"F14.wireOp",EDGE,"E150")}),-1.0]])]});
            var Q6;
            Q6=makeQuery(id+"F14.imprint","IMPRINT",FACE,{"disambiguationData":[TD([[makeQuery(id+"F14.imprint","IMPRINT",EDGE,{"derivedFrom":sQuery(id+"F14.wireOp",EDGE,"E157.1.0.0")}),1.0]])]});
            var Q7;
            Q7=makeQuery(id+"F14.imprint","IMPRINT",FACE,{"disambiguationData":[TD([[makeQuery(id+"F14.imprint","IMPRINT",EDGE,{"derivedFrom":sQuery(id+"F14.wireOp",EDGE,"E157.2.0.0")}),1.0]])]});
            var Q8;
            Q8=makeQuery(id+"F14.imprint","IMPRINT",FACE,{"disambiguationData":[TD([[makeQuery(id+"F14.imprint","IMPRINT",EDGE,{"derivedFrom":sQuery(id+"F14.wireOp",EDGE,"E171.MirrorCS")}),-1.0]])]});
            var Q9;
            Q9=makeQuery(id+"F14.imprint","IMPRINT",FACE,{"disambiguationData":[TD([[makeQuery(id+"F14.imprint","IMPRINT",EDGE,{"derivedFrom":sQuery(id+"F14.wireOp",EDGE,"E173.MirrorCS")}),1.0]])]});
            var Q10;
            Q10=makeQuery(id+"F14.imprint","IMPRINT",FACE,{"disambiguationData":[TD([[makeQuery(id+"F14.imprint","IMPRINT",EDGE,{"derivedFrom":sQuery(id+"F14.wireOp",EDGE,"E159.2.0.0")}),-1.0]])]});
            extrude(context, id + "F16", {"entities" : qUnion([Q0, Q1, Q2, Q3, Q4, Q5, Q6, Q7, Q8, Q9, Q10]), "operationType" : NewBodyOperationType.ADD, "depth" : 4.4 * mm, "offsetDistance" : 25 * mm});
        }
        {
            var Q0;
            Q0=makeQuery(id+"F15.opExtrude","CAP_EDGE",EDGE,{"disambiguationData":[OSD([sQuery(id+"F14.wireOp",EDGE,"E141.0.1.0")])],"isStart":false});
            var Q1;
            Q1=makeQuery(id+"F15.opExtrude","CAP_EDGE",EDGE,{"disambiguationData":[OSD([sQuery(id+"F14.wireOp",EDGE,"E140")])],"isStart":false});
            var Q2;
            Q2=makeQuery(id+"F15.opExtrude","CAP_EDGE",EDGE,{"disambiguationData":[OSD([sQuery(id+"F14.wireOp",EDGE,"E141.1.0.0")])],"isStart":false});
            var Q3;
            Q3=makeQuery(id+"F15.opExtrude","CAP_EDGE",EDGE,{"disambiguationData":[OSD([sQuery(id+"F14.wireOp",EDGE,"E141.1.1.0")])],"isStart":false});
            chamfer(context, id + "F17", {"entities" : qUnion([Q0, Q1, Q2, Q3]), "chamferType" : ChamferType.OFFSET_ANGLE, "width" : .6 * mm, "oppositeDirection" : false, "angle" : 45 * degree, "tangentPropagation" : true});
        }
    });
